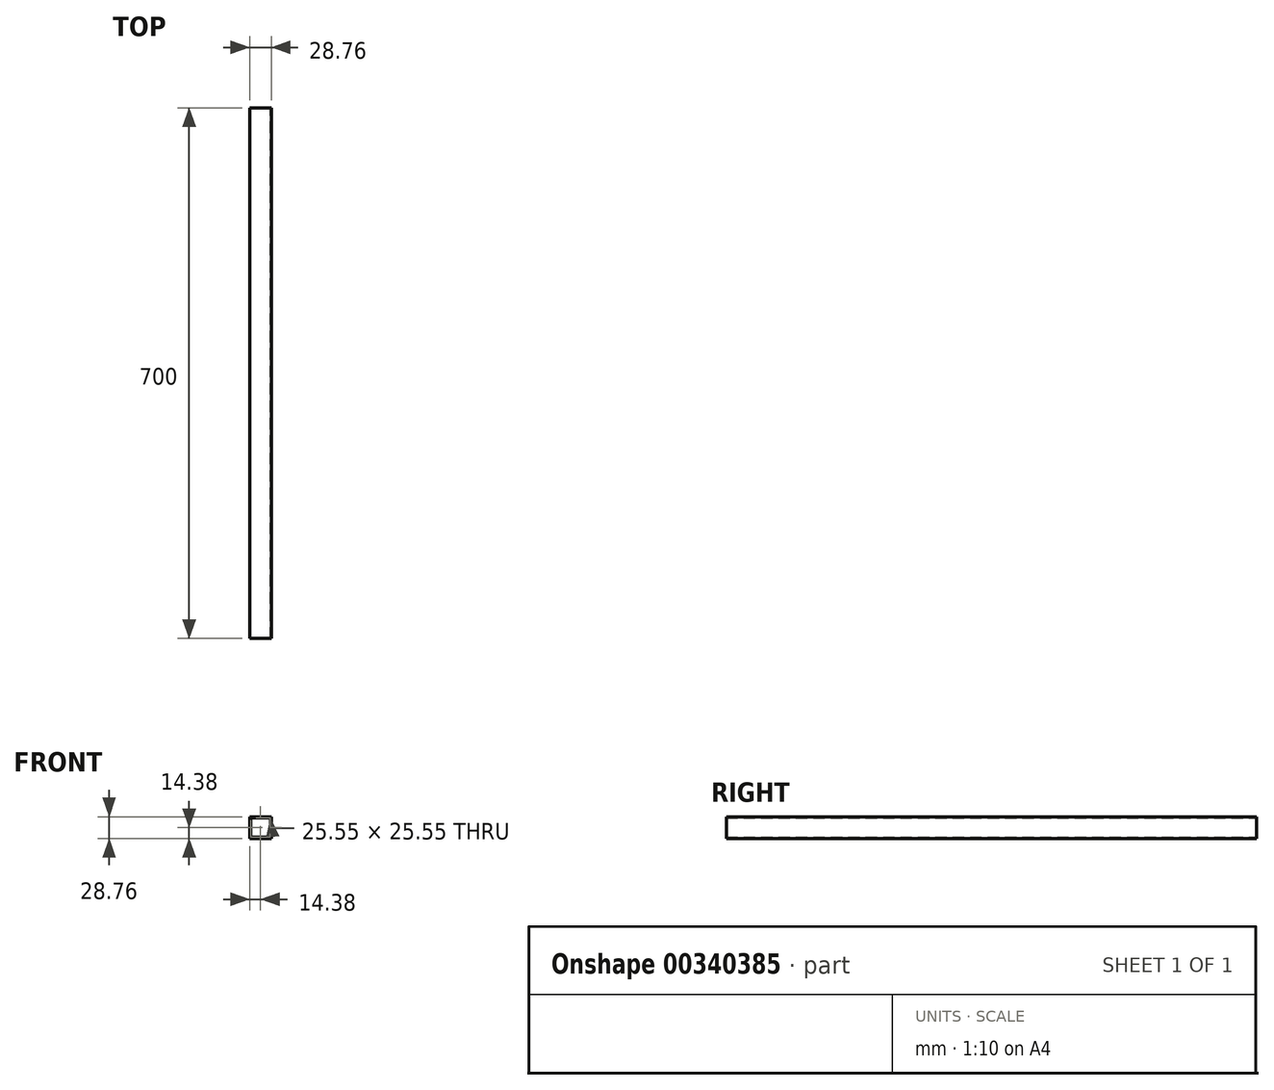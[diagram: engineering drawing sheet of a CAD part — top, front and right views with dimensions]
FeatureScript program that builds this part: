
annotation { "Feature Type Name" : "Feature", "Feature Type Description" : "" }
export const myFeature = defineFeature(function(context is Context, id is Id, definition is map)
    precondition{}
    {
        {
            var Q0;
            Q0=qCreatedBy(makeId("Front.planeOp"),FACE);
            var sketch = newSketch(context, id + "F0", { "sketchPlane" : qUnion([Q0])});
            skLineSegment(sketch, "E0.bottom", {"start": v(14.37, 14.38) * mm, "end": v(-14.38, 14.38) * mm});
            skLineSegment(sketch, "E0.top", {"start": v(14.38, -14.38) * mm, "end": v(-14.37, -14.38) * mm});
            skLineSegment(sketch, "E0.left", {"start": v(14.37, 14.37) * mm, "end": v(14.38, -14.38) * mm});
            skLineSegment(sketch, "E0.right", {"start": v(-14.38, 14.38) * mm, "end": v(-14.37, -14.38) * mm});
            skPoint(sketch, "E0.middle", {"position": v(0, 0) * mm});
            skSolve(sketch);
        }
        {
            var Q0;
            Q0=makeQuery(id+"F0.imprint","IMPRINT",FACE,{"disambiguationData":[TD([[makeQuery(id+"F0.imprint","IMPRINT",EDGE,{"derivedFrom":sQuery(id+"F0.wireOp",EDGE,"E0.bottom")}),1.0]])]});
            extrude(context, id + "F1", {"entities" : qUnion([Q0]), "depth" : 700 * mm});
        }
        {
            var Q0;
            Q0=makeQuery(id+"F1.opExtrude","CAP_FACE",FACE,{"disambiguationData":[OSD([sQuery(id+"F0.wireOp",EDGE,"E0.bottom"),sQuery(id+"F0.wireOp",EDGE,"E0.top"),sQuery(id+"F0.wireOp",EDGE,"E0.left"),sQuery(id+"F0.wireOp",EDGE,"E0.right")])],"isStart":true});
            var Q1;
            Q1=makeQuery(id+"F1.opExtrude","CAP_FACE",FACE,{"disambiguationData":[OSD([sQuery(id+"F0.wireOp",EDGE,"E0.bottom"),sQuery(id+"F0.wireOp",EDGE,"E0.top"),sQuery(id+"F0.wireOp",EDGE,"E0.left"),sQuery(id+"F0.wireOp",EDGE,"E0.right")])],"isStart":false});
            shell(context, id + "F2", {"entities" : qUnion([Q0, Q1]), "thickness" : 1.6 * mm});
        }
    });
